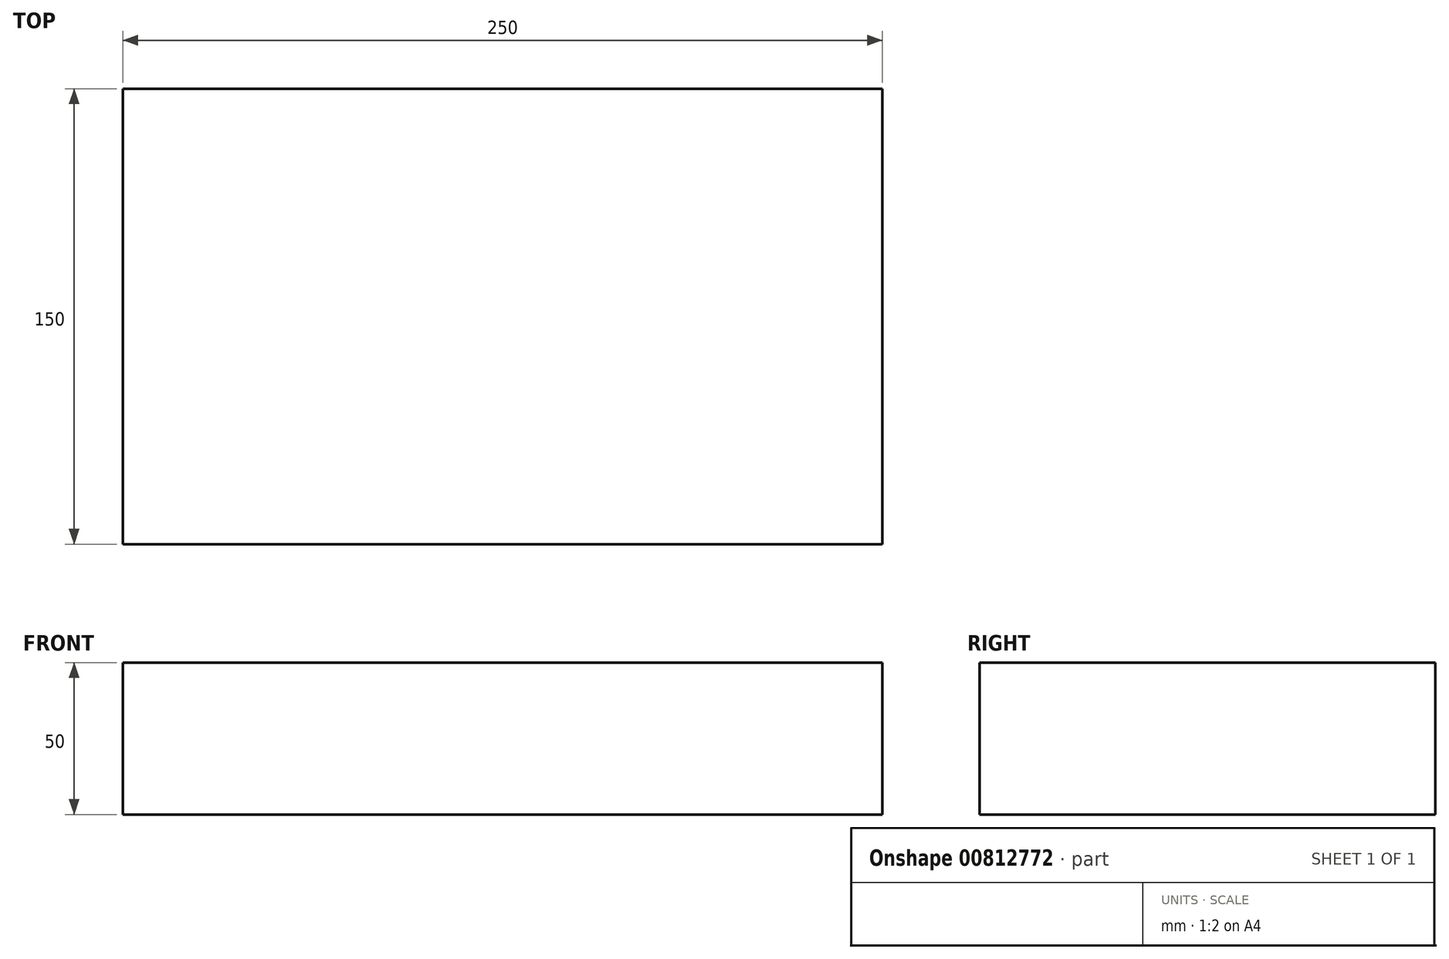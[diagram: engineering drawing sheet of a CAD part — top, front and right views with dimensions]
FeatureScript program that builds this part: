
annotation { "Feature Type Name" : "Feature", "Feature Type Description" : "" }
export const myFeature = defineFeature(function(context is Context, id is Id, definition is map)
    precondition{}
    {
        {
            var Q0;
            Q0=qCreatedBy(makeId("Top.planeOp"),FACE);
            var sketch = newSketch(context, id + "F0", { "sketchPlane" : qUnion([Q0])});
            skLineSegment(sketch, "E0.bottom", {"start": v(0, 0) * mm, "end": v(250, 0) * mm});
            skLineSegment(sketch, "E0.top", {"start": v(0, 150) * mm, "end": v(250, 150) * mm});
            skLineSegment(sketch, "E0.left", {"start": v(0, 0) * mm, "end": v(0, 150) * mm});
            skLineSegment(sketch, "E0.right", {"start": v(250, 0) * mm, "end": v(250, 150) * mm});
            skSolve(sketch);
        }
        {
            var Q0;
            Q0=makeQuery(id+"F0.imprint","IMPRINT",FACE,{"disambiguationData":[TD([[makeQuery(id+"F0.imprint","IMPRINT",EDGE,{"derivedFrom":sQuery(id+"F0.wireOp",EDGE,"E0.bottom")}),1.0]])]});
            extrude(context, id + "F1", {"entities" : qUnion([Q0]), "depth" : 50 * mm, "offsetDistance" : 25 * mm});
        }
    });
